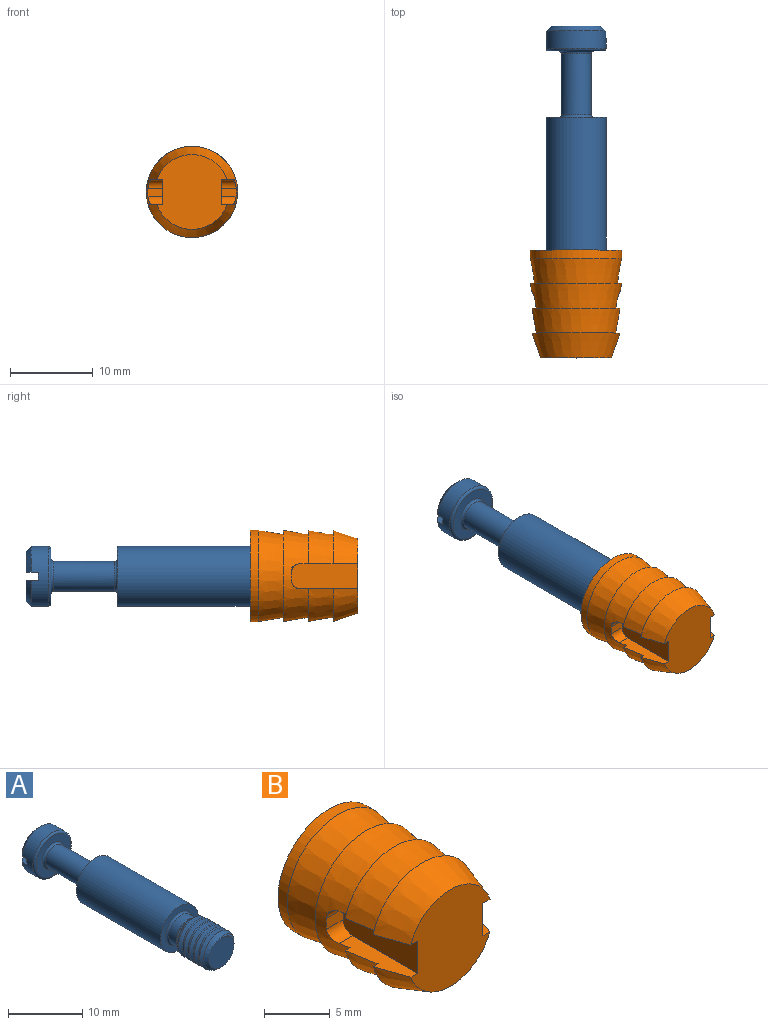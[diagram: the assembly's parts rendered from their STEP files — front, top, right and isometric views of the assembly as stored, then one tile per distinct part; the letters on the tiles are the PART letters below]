
ASSEMBLY  parts=2 mates=1
PART A: 27 faces, bbox 7.8x35.4x7.8 mm
  f0: cylinder r=3.6mm len=7.2mm, axis (0,-1,0), area 45.7mm2, adj f2,f16,f21,f24,f25,f26
  f1: plane 5.92x2.5mm, normal (0,1,0), area 11.2mm2, adj f21,f25
  f2: cone r=3.6mm half-angle=45deg, axis (0,-1,0), area 7.9mm2, adj f0,f11,f24
  f3: plane 6.6x6.6mm, normal (0,-1,0), area 20.4mm2, adj f16,f17
  f4: cylinder r=1.8mm len=7.4mm, axis (0,-1,0), area 83.7mm2, adj f17,f18
  f5: plane 7.2x7.2mm, normal (0,1,0), area 26.9mm2, adj f6,f18
  f6: cylinder r=3.6mm len=16mm, axis (0,-1,0), area 361.9mm2, adj f5,f7
  f7: plane 7.2x7.2mm, normal (0,-1,0), area 19.5mm2, adj f6,f19
  f8: cylinder r=2.3mm len=4.6mm, axis (0,-1,0), area 20.2mm2, adj f19,f20
  f9: cylinder r=3mm len=6mm, axis (0,-1,0), area 26.3mm2, adj f13,f15,f22,f23
  f10: plane 4.8x4.8mm, normal (0,-1,0), area 18.1mm2, adj f14,f15,f23
  f11: plane 5.92x2.5mm, normal (0,1,0), area 11.2mm2, adj f2,f24
  f12: plane 0.28x0.2mm, normal (-1,0,0), area 0mm2, adj f13,f15,f20,f22
  f13: bspline ~6.93x6.36mm, area 65.9mm2, adj f9,f12,f14,f15,f20,f22,f23
  f14: plane 0.05x0.03mm, normal (1,0,0), area 0mm2, adj f10,f13,f15,f23
  f15: bspline ~6.93x6.36mm, area 65.6mm2, adj f9,f10,f12,f13,f14,f22,f23
  f16: torus R=3.3mm, axis (0,1,0), area 10.3mm2, adj f0,f3
  f17: torus R=2.1mm, axis (0,1,0), area 5.7mm2, adj f3,f4
  f18: torus R=2.1mm, axis (0,-1,0), area 5.7mm2, adj f4,f5
  f19: torus R=2.6mm, axis (0,1,0), area 7.1mm2, adj f7,f8
  f20: torus R=2.6mm, axis (0,-1,0), area 6mm2, adj f8,f12,f13,f22
  f21: cone r=3.6mm half-angle=45deg, axis (0,-1,0), area 7.9mm2, adj f0,f1,f25
  f22: cone r=3mm half-angle=38.6deg, axis (0,-1,0), area 7.4mm2, adj f9,f12,f13,f15,f20
  f23: cone r=2.4mm half-angle=45deg, axis (0,1,0), area 9mm2, adj f9,f10,f13,f14,f15
  f24: plane 7.14x1.51mm, normal (0,0,1), area 10.3mm2, adj f0,f2,f11,f26
  f25: plane 7.14x1.51mm, normal (0,0,-1), area 10.3mm2, adj f0,f1,f21,f26
  f26: plane 7.2x1mm, normal (0,1,0), area 7.2mm2, adj f0,f24,f25
PART B: 34 faces, bbox 11.2x13.5x11.2 mm
  f0: plane 6.74x6.74mm, normal (0,-1,0), area 12.3mm2, adj f1,f17,f30,f33
  f1: cylinder r=2.5mm len=9mm, axis (0,-1,0), area 62.8mm2, adj f0,f12,f30,f31,f32,f33
  f2: cone r=5mm half-angle=9.5deg, axis (0,1,0), area 90mm2, adj f3,f4,f15,f19,f20,f21,f22,f23
  f3: plane 10.56x3.96mm, normal (0,1,0), area 6.7mm2, adj f2,f5,f20,f22
  f4: plane 10.6x4.04mm, normal (0,1,0), area 6.8mm2, adj f2,f6,f19,f23
  f5: cone r=5mm half-angle=9.5deg, axis (0,1,0), area 40.7mm2, adj f3,f7,f20,f22
  f6: cone r=5mm half-angle=9.5deg, axis (0,1,0), area 41.1mm2, adj f4,f8,f19,f23
  f7: plane 10.56x3.96mm, normal (0,1,0), area 6.7mm2, adj f5,f9,f20,f22
  f8: plane 10.6x4.04mm, normal (0,1,0), area 6.8mm2, adj f6,f10,f19,f23
  f9: cone r=4.5mm half-angle=18.4deg, axis (0,1,0), area 39.7mm2, adj f7,f11,f20,f22
  f10: cone r=4.5mm half-angle=18.4deg, axis (0,1,0), area 40.2mm2, adj f8,f11,f19,f23
  f11: plane 9x8.51mm, normal (0,-1,0), area 58.1mm2, adj f9,f10,f18,f19,f20,f22,f23,f24
  f12: plane 11.24x11.24mm, normal (0,1,0), area 74.2mm2, adj f1,f13,f31,f32
  f13: cylinder r=5.5mm len=11mm, axis (0,-1,0), area 34.6mm2, adj f12,f14
  f14: cone r=5mm half-angle=9.5deg, axis (0,1,0), area 100.3mm2, adj f13,f15
  f15: plane 11x11mm, normal (0,1,0), area 16.5mm2, adj f2,f14
  f16: plane 6.5x6.5mm, normal (0,1,0), area 33.2mm2, adj f17
  f17: cylinder r=3.25mm len=6.5mm, axis (0,-1,0), area 28.8mm2, adj f0,f16
  f18: plane 8x3mm, normal (-1,0,0), area 23.6mm2, adj f11,f19,f20,f21,f26,f27
  f19: plane 7.03x1.83mm, normal (0,0,-1), area 9.8mm2, adj f2,f4,f6,f8,f10,f11,f18,f27
  f20: plane 7.03x1.82mm, normal (0,0,1), area 9.7mm2, adj f2,f3,f5,f7,f9,f11,f18,f26
  f21: plane 1.83x1mm, normal (0,-1,0), area 1.8mm2, adj f2,f18,f26,f27
  f22: plane 7.03x1.82mm, normal (0,0,1), area 9.7mm2, adj f2,f3,f5,f7,f9,f11,f24,f29
  f23: plane 7.03x1.83mm, normal (0,0,-1), area 9.8mm2, adj f2,f4,f6,f8,f10,f11,f24,f28
  f24: plane 8x3mm, normal (1,0,0), area 23.6mm2, adj f11,f22,f23,f25,f28,f29
  f25: plane 1.83x1mm, normal (0,-1,0), area 1.8mm2, adj f2,f24,f28,f29
  f26: cylinder r=1mm len=1.81mm, axis (1,0,0), area 2.5mm2, adj f2,f18,f20,f21
  f27: cylinder r=1mm len=1.81mm, axis (-1,0,0), area 2.6mm2, adj f2,f18,f19,f21
  f28: cylinder r=1mm len=1.81mm, axis (-1,0,0), area 2.6mm2, adj f2,f23,f24,f25
  f29: cylinder r=1mm len=1.81mm, axis (1,0,0), area 2.5mm2, adj f2,f22,f24,f25
  f30: plane 0.5x0.29mm, normal (1,0,0), area 0.1mm2, adj f0,f1,f32
  f31: plane 0.5x0.29mm, normal (-1,0,0), area 0.1mm2, adj f1,f12,f33
  f32: bspline ~9.29x6.93mm, area 88.2mm2, adj f1,f12,f30,f33
  f33: bspline ~9.29x6.93mm, area 88.9mm2, adj f0,f1,f31,f32
PLACE A t=(0.02,24,-0.03)mm
PLACE B at identity fixed
MATE fastened B.f12 <-> A.f0  axis (0,1,0) through (0.02,0,-0.03)mm
